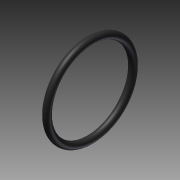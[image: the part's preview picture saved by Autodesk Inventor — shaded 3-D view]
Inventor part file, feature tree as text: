
AUTODESK INVENTOR PART (.ipt)
format: ipt  version: 2012 SP1 (Build 160190100, 190)  size: 125,952 bytes
history: native  units: in
note: dims shown in document units (in); Inventor stores cm internally (conversion verified against a paired STEP export)
features: sketch x2, sweep x1
ambient origin geometry x8: Origin, YZ Plane, XZ Plane, XY Plane, X Axis, Y Axis, Z Axis, Center Point
bodies: Solid1 (feature_tree)
feature tree (3):
  sweep  "Sweep1"
  sketch  "Sketch1"  dims[d0=0.103in d1=1.174in]
  sketch  "Sketch2"  dims[d3=0.0in]
